# Revit family: equip-water-cooler-hlsy-tylr-hvr-hd
name_source: partatom
category: Plumbing Fixtures
units: mm (PartAtom-declared; Revit-internal decimal feet)

## family parameters
Always vertical = Yes
Cut with Voids When Loaded = No
OmniClass Number = 23.45.00.00
OmniClass Title = Sanitary, Laundry, and Cleaning Equipment
Part Type = Normal
Room Calculation Point = No
Round Connector Dimension = Use Radius
Shared = No
Work Plane-Based = No

## types (2) — shared parameters
Activation = VR Pushbutton
Apparent Load Phase 1 = 0 VA
Basin Material = Metal - Steel - Stainless - Chrome
Bubbler = VR Bubbler
CW Connection = Yes
Cooler Depth = 1' - 6 9/16"
Cooler Height = 1' - 8 7/16"
Cooler Width = 3' - 0 1/2"
Description = ADA Vandal Resistant Cooler
Dispenser Height = 2' - 3"
Filter = **ACC (HWF172)
HW Connection = No
Louver Screens = -
Manufacturer = halseytaylor
Number of Poles = 1
Orifice Height = 2' - 8 9/16"
Other Features = All include VR pinned torx screws
Panel Material = Metal - Steel - Stainless - Chrome
Rim Height = 2' - 7 1/2"
Sanitary Connector Description = Sanitary Connection
Sanitary Service Radius = 0' - 0"
Sanitary Service Size Radius = 0' - 0 5/8"
Specification = http://www.halseytaylor.com
Type = Single
URL = http://www.halseytaylor.com
Vent Connection = No
Version = 1.0.0.0
Waste Connection = Yes
Water Connector Description = Water Supply
Water Service Flow = 0 GPM
Water Service Size Radius = 0' - 0 1/4"
zero-valued in all types: Power Factor

## per-type parameters (varying)
| type | Refrigerated | Volts/Hertz |
| HVR8HD 14GA ADA VR CLR | Yes | 115V/60Hz |
| HVRDHD 14GA ADA VR L/R | No |  |

note: column(s) folded — value = type name in every type: Model

## geometry (parser evidence)
native form markers: Sweep x5
no freeform markers — native parametric forms only
